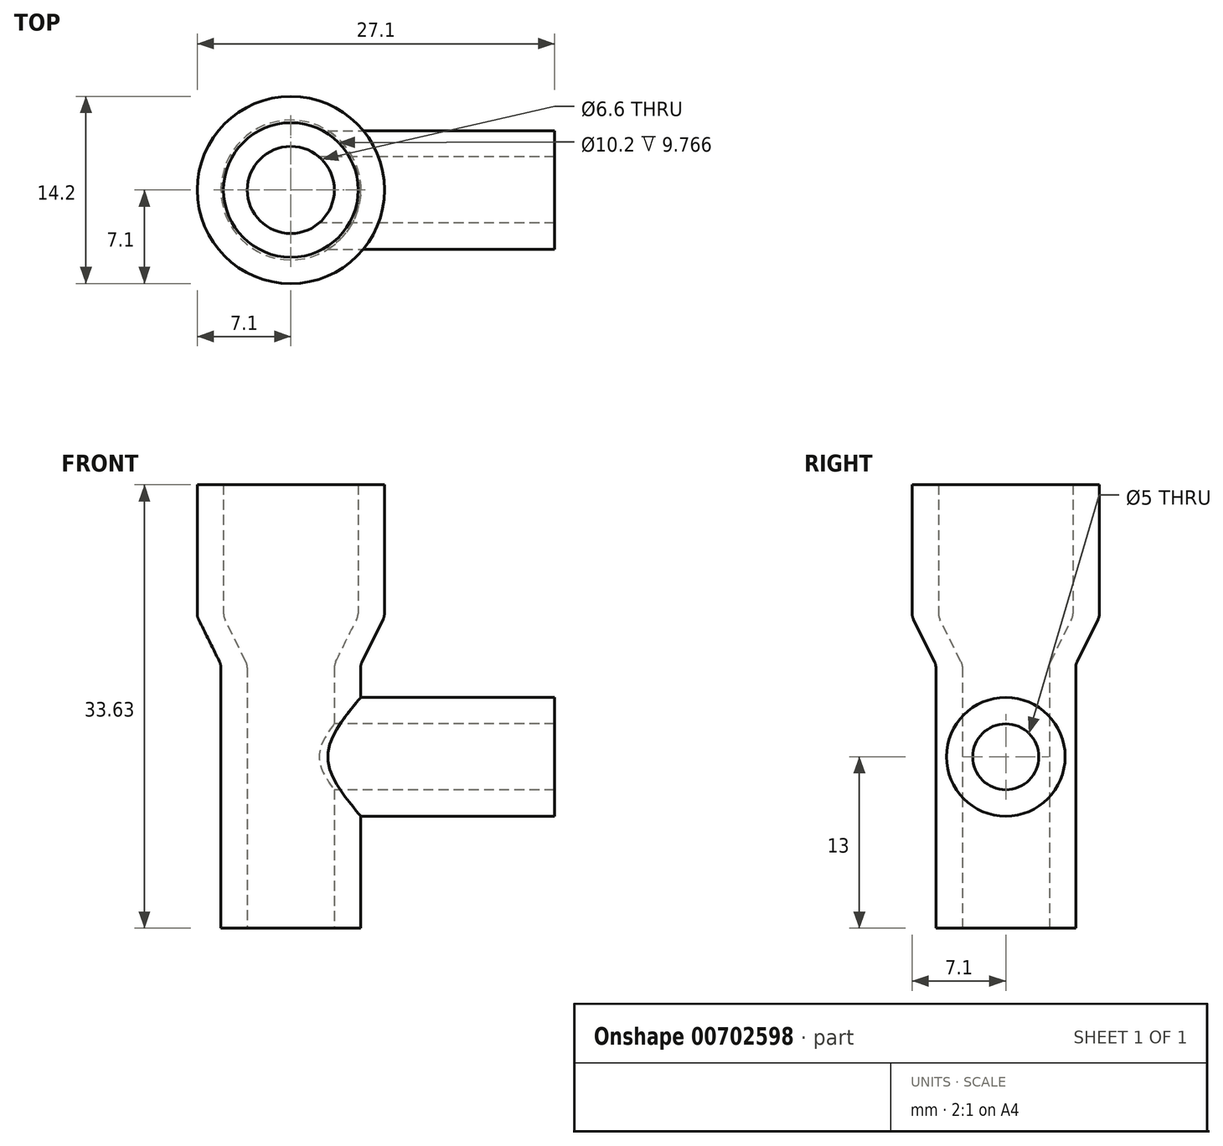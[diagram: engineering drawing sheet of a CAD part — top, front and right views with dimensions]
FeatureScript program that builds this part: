
annotation { "Feature Type Name" : "Feature", "Feature Type Description" : "" }
export const myFeature = defineFeature(function(context is Context, id is Id, definition is map)
    precondition{}
    {
        {
            var Q0;
            Q0=qCreatedBy(makeId("Front.planeOp"),FACE);
            var sketch = newSketch(context, id + "F0", { "sketchPlane" : qUnion([Q0])});
            skLineSegment(sketch, "E0", {"start": v(-5.3, 0) * mm, "end": v(-5.3, 20) * mm});
            skLineSegment(sketch, "E1", {"start": v(-7.1, 33.63) * mm, "end": v(-7.1, 23.63) * mm});
            skLineSegment(sketch, "E2", {"start": v(-7.1, 23.63) * mm, "end": v(-5.3, 20) * mm});
            skLineSegment(sketch, "E3", {"start": v(-3.3, 0) * mm, "end": v(-3.3, 20) * mm});
            skLineSegment(sketch, "E4", {"start": v(-5.1, 33.63) * mm, "end": v(-5.1, 23.63) * mm});
            skLineSegment(sketch, "E5", {"start": v(-5.1, 23.63) * mm, "end": v(-3.3, 20) * mm});
            skLineSegment(sketch, "E6", {"start": v(-5.3, 0) * mm, "end": v(-3.3, 0) * mm});
            skLineSegment(sketch, "E7", {"start": v(-7.1, 33.63) * mm, "end": v(-5.1, 33.63) * mm});
            skLineSegment(sketch, "E8", {"start": v(0, 0) * mm, "end": v(0, 20.2) * mm, "construction": true});
            skSolve(sketch);
        }
        {
            var Q0;
            Q0=makeQuery(id+"F0.imprint","IMPRINT",FACE,{"disambiguationData":[TD([[makeQuery(id+"F0.imprint","IMPRINT",EDGE,{"derivedFrom":sQuery(id+"F0.wireOp",EDGE,"E0")}),-1.0]])]});
            var Q1;
            Q1=sQuery(id+"F0.wireOp",EDGE,"E8");
            revolve(context, id + "F1", {"entities" : qUnion([Q0]), "axis" : qUnion([Q1]), "revolveType" : RevolveType.FULL});
        }
        {
            var Q0;
            Q0=qCreatedBy(makeId("Right.planeOp"),FACE);
            var sketch = newSketch(context, id + "F2", { "sketchPlane" : qUnion([Q0])});
            skCircle(sketch, "E9", {"center": v(0, 13) * mm, "radius": 2.5 * mm});
            skSolve(sketch);
        }
        {
            var Q0;
            Q0 = qSketchRegion(id + "F2", true);
            var Q1;
            Q1=makeQuery(id+"F1.opRevolve","SWEPT_FACE",FACE,{"disambiguationData":[OSD([sQuery(id+"F0.wireOp",EDGE,"E0")])]});
            extrude(context, id + "F3", {"entities" : qUnion([Q0]), "operationType" : NewBodyOperationType.REMOVE, "endBound" : BoundingType.UP_TO_SURFACE, "depth" : 25 * mm, "endBoundEntityFace" : qUnion([Q1]), "offsetDistance" : 25 * mm});
        }
        {
            var Q0;
            Q0=qCreatedBy(makeId("Right.planeOp"),FACE);
            cPlane(context, id + "F4", {"entities" : qUnion([Q0]), "cplaneType" : CPlaneType.OFFSET, "offset" : 20 * mm, "width" : 150 * mm, "height" : 150 * mm});
        }
        {
            var Q0;
            Q0=qCreatedBy(id+"F4.planeOp",FACE);
            var sketch = newSketch(context, id + "F5", { "sketchPlane" : qUnion([Q0])});
            skCircle(sketch, "E10", {"center": v(0, 13) * mm, "radius": 2.5 * mm});
            skCircle(sketch, "E11", {"center": v(0, 13) * mm, "radius": 4.5 * mm});
            skSolve(sketch);
        }
        {
            var Q0;
            Q0 = qSketchRegion(id + "F5", true);
            var Q1;
            Q1=makeQuery(id+"F1.opRevolve","SWEPT_FACE",FACE,{"disambiguationData":[OSD([sQuery(id+"F0.wireOp",EDGE,"E0")])]});
            extrude(context, id + "F6", {"entities" : qUnion([Q0]), "operationType" : NewBodyOperationType.ADD, "endBound" : BoundingType.UP_TO_SURFACE, "oppositeDirection" : true, "depth" : 25 * mm, "endBoundEntityFace" : qUnion([Q1]), "offsetDistance" : 25 * mm});
        }
        {
            var Q0;
            Q0=makeQuery(id+"F1.opRevolve","SWEPT_EDGE",EDGE,{"disambiguationData":[OSD([sQuery(id+"F0.wireOp",EDGE,"E0"),sQuery(id+"F0.wireOp",EDGE,"E2")])]});
            var Q1;
            Q1=makeQuery(id+"F1.opRevolve","SWEPT_EDGE",EDGE,{"disambiguationData":[OSD([sQuery(id+"F0.wireOp",EDGE,"E1"),sQuery(id+"F0.wireOp",EDGE,"E2")])]});
            var Q2;
            Q2=makeQuery(id+"F6.opExtrude","TWEAK_EDGE",EDGE,{"derivedFrom":[makeQuery(id+"F1.opRevolve","SWEPT_FACE",FACE,{"disambiguationData":[OSD([sQuery(id+"F0.wireOp",EDGE,"E0")])]}),makeQuery(id+"F5.imprint","IMPRINT",EDGE,{"derivedFrom":sQuery(id+"F5.wireOp",EDGE,"E11")})]});
            var Q3;
            Q3=makeQuery(id+"F1.opRevolve","SWEPT_EDGE",EDGE,{"disambiguationData":[OSD([sQuery(id+"F0.wireOp",EDGE,"E4"),sQuery(id+"F0.wireOp",EDGE,"E5")])]});
            var Q4;
            Q4=makeQuery(id+"F1.opRevolve","SWEPT_EDGE",EDGE,{"disambiguationData":[OSD([sQuery(id+"F0.wireOp",EDGE,"E3"),sQuery(id+"F0.wireOp",EDGE,"E5")])]});
            fillet(context, id + "F7", {"entities" : qUnion([Q0, Q1, Q2, Q3, Q4]), "radius" : 1 * mm, "tangentPropagation" : true, "allowEdgeOverflow" : false});
        }
    });
